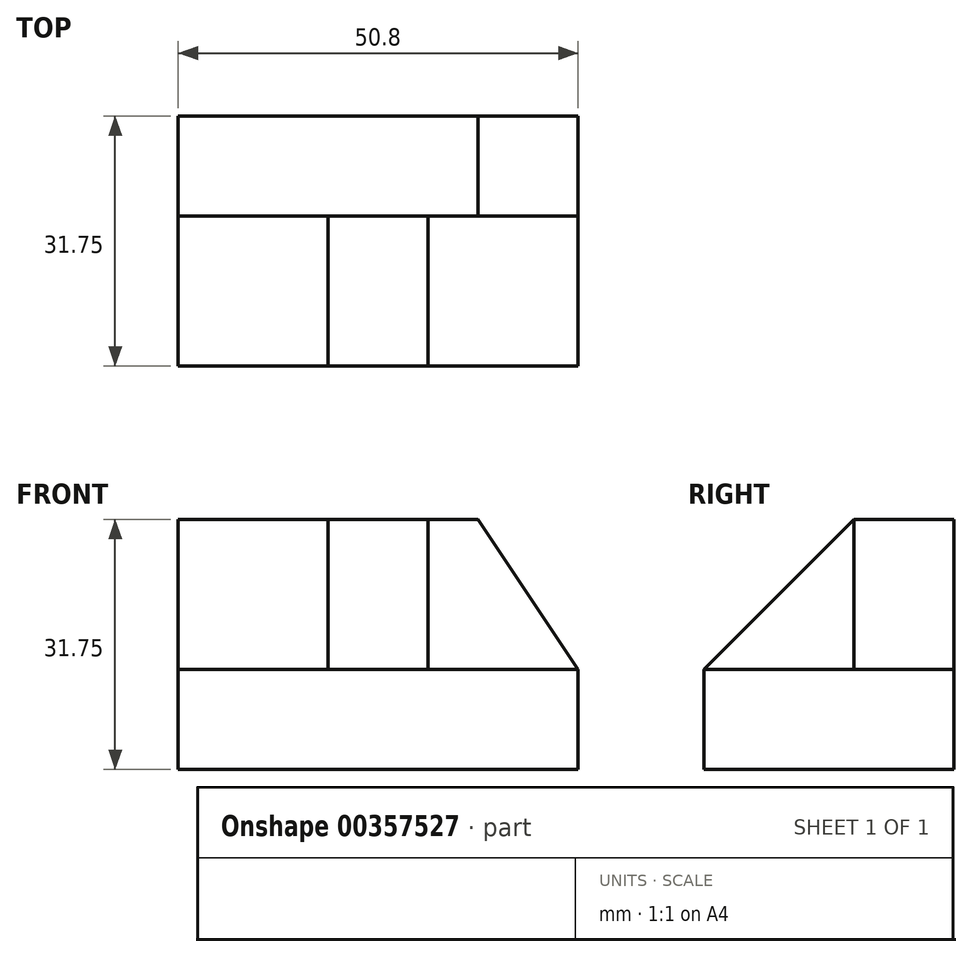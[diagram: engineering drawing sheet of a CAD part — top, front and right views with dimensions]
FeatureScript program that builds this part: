
annotation { "Feature Type Name" : "Feature", "Feature Type Description" : "" }
export const myFeature = defineFeature(function(context is Context, id is Id, definition is map)
    precondition{}
    {
        {
            var Q0;
            Q0=qCreatedBy(makeId("Right.planeOp"),FACE);
            var sketch = newSketch(context, id + "F0", { "sketchPlane" : qUnion([Q0])});
            skLineSegment(sketch, "E0", {"start": v(-51.82, 44.2) * mm, "end": v(-51.82, 12.44) * mm});
            skLineSegment(sketch, "E1", {"start": v(-51.82, 12.44) * mm, "end": v(-20.07, 12.44) * mm});
            skLineSegment(sketch, "E2", {"start": v(-20.07, 12.44) * mm, "end": v(-20.07, 44.2) * mm});
            skLineSegment(sketch, "E3", {"start": v(-20.07, 44.2) * mm, "end": v(-51.82, 44.2) * mm});
            skSolve(sketch);
        }
        {
            var Q0;
            Q0 = qSketchRegion(id + "F0", true);
            extrude(context, id + "F1", {"entities" : qUnion([Q0]), "depth" : 50.8 * mm});
        }
        {
            var Q0;
            Q0=makeQuery(id+"F1.opExtrude","SWEPT_FACE",FACE,{"disambiguationData":[OSD([sQuery(id+"F0.wireOp",EDGE,"E0")])]});
            var sketch = newSketch(context, id + "F2", { "sketchPlane" : qUnion([Q0])});
            skLineSegment(sketch, "E4", {"start": v(0, 25.14) * mm, "end": v(50.8, 25.14) * mm});
            skLineSegment(sketch, "E5", {"start": v(50.8, 25.14) * mm, "end": v(50.8, 44.2) * mm});
            skLineSegment(sketch, "E6", {"start": v(50.8, 44.2) * mm, "end": v(0, 44.2) * mm});
            skLineSegment(sketch, "E7", {"start": v(0, 44.2) * mm, "end": v(0, 25.14) * mm});
            skSolve(sketch);
        }
        {
            var Q0;
            Q0=makeQuery(id+"F2.imprint","IMPRINT",FACE,{"disambiguationData":[TD([[makeQuery(id+"F2.imprint","IMPRINT",EDGE,{"derivedFrom":sQuery(id+"F2.wireOp",EDGE,"E4")}),1.0]])]});
            extrude(context, id + "F3", {"entities" : qUnion([Q0]), "operationType" : NewBodyOperationType.REMOVE, "oppositeDirection" : true, "depth" : 19.05 * mm});
        }
        {
            var Q0;
            Q0=makeQuery(id+"F3.boolean.opBoolean","COPY",FACE,{"derivedFrom":makeQuery(id+"F3.opExtrude","CAP_FACE",FACE,{"disambiguationData":[OSD([sQuery(id+"F2.wireOp",EDGE,"E4"),sQuery(id+"F2.wireOp",EDGE,"E5"),sQuery(id+"F2.wireOp",EDGE,"E6"),sQuery(id+"F2.wireOp",EDGE,"E7")])],"isStart":false})});
            var sketch = newSketch(context, id + "F4", { "sketchPlane" : qUnion([Q0])});
            skLineSegment(sketch, "E8", {"start": v(50.8, 44.2) * mm, "end": v(50.8, 25.14) * mm});
            skLineSegment(sketch, "E9", {"start": v(50.8, 44.2) * mm, "end": v(38.1, 44.2) * mm});
            skLineSegment(sketch, "E10", {"start": v(38.1, 44.2) * mm, "end": v(50.8, 25.14) * mm});
            skSolve(sketch);
        }
        {
            var Q0;
            Q0 = qSketchRegion(id + "F4", true);
            extrude(context, id + "F5", {"entities" : qUnion([Q0]), "operationType" : NewBodyOperationType.REMOVE, "oppositeDirection" : true, "depth" : 12.7 * mm});
        }
        {
            var Q0;
            Q0=makeQuery(id+"F1.opExtrude","SWEPT_FACE",FACE,{"disambiguationData":[OSD([sQuery(id+"F0.wireOp",EDGE,"E3")])]});
            var sketch = newSketch(context, id + "F6", { "sketchPlane" : qUnion([Q0])});
            skLineSegment(sketch, "E11", {"start": v(19.05, -32.77) * mm, "end": v(19.05, -51.82) * mm});
            skLineSegment(sketch, "E12", {"start": v(19.05, -51.82) * mm, "end": v(31.75, -51.82) * mm});
            skLineSegment(sketch, "E13", {"start": v(31.75, -51.82) * mm, "end": v(31.75, -32.77) * mm});
            skLineSegment(sketch, "E14", {"start": v(19.05, -32.77) * mm, "end": v(0, -32.77) * mm});
            skLineSegment(sketch, "E15", {"start": v(19.05, -32.77) * mm, "end": v(31.75, -32.77) * mm});
            skSolve(sketch);
        }
        {
            var Q0;
            Q0=makeQuery(id+"F6.imprint","IMPRINT",FACE,{"disambiguationData":[TD([[makeQuery(id+"F6.imprint","IMPRINT",EDGE,{"derivedFrom":sQuery(id+"F6.wireOp",EDGE,"E11")}),1.0]])]});
            extrude(context, id + "F7", {"entities" : qUnion([Q0]), "operationType" : NewBodyOperationType.ADD, "oppositeDirection" : true, "depth" : 19.05 * mm});
        }
        {
            var Q0;
            Q0=makeQuery(id+"F7.opExtrude","SWEPT_FACE",FACE,{"disambiguationData":[OSD([sQuery(id+"F6.wireOp",EDGE,"E11")])]});
            var sketch = newSketch(context, id + "F8", { "sketchPlane" : qUnion([Q0])});
            skLineSegment(sketch, "E16", {"start": v(32.77, 44.2) * mm, "end": v(51.82, 25.14) * mm});
            skLineSegment(sketch, "E17", {"start": v(32.77, 44.2) * mm, "end": v(51.82, 44.2) * mm});
            skLineSegment(sketch, "E18", {"start": v(51.82, 44.2) * mm, "end": v(51.82, 25.14) * mm});
            skSolve(sketch);
        }
        {
            var Q0;
            Q0 = qSketchRegion(id + "F8", true);
            extrude(context, id + "F9", {"entities" : qUnion([Q0]), "operationType" : NewBodyOperationType.REMOVE, "oppositeDirection" : true, "depth" : 12.7 * mm});
        }
    });
